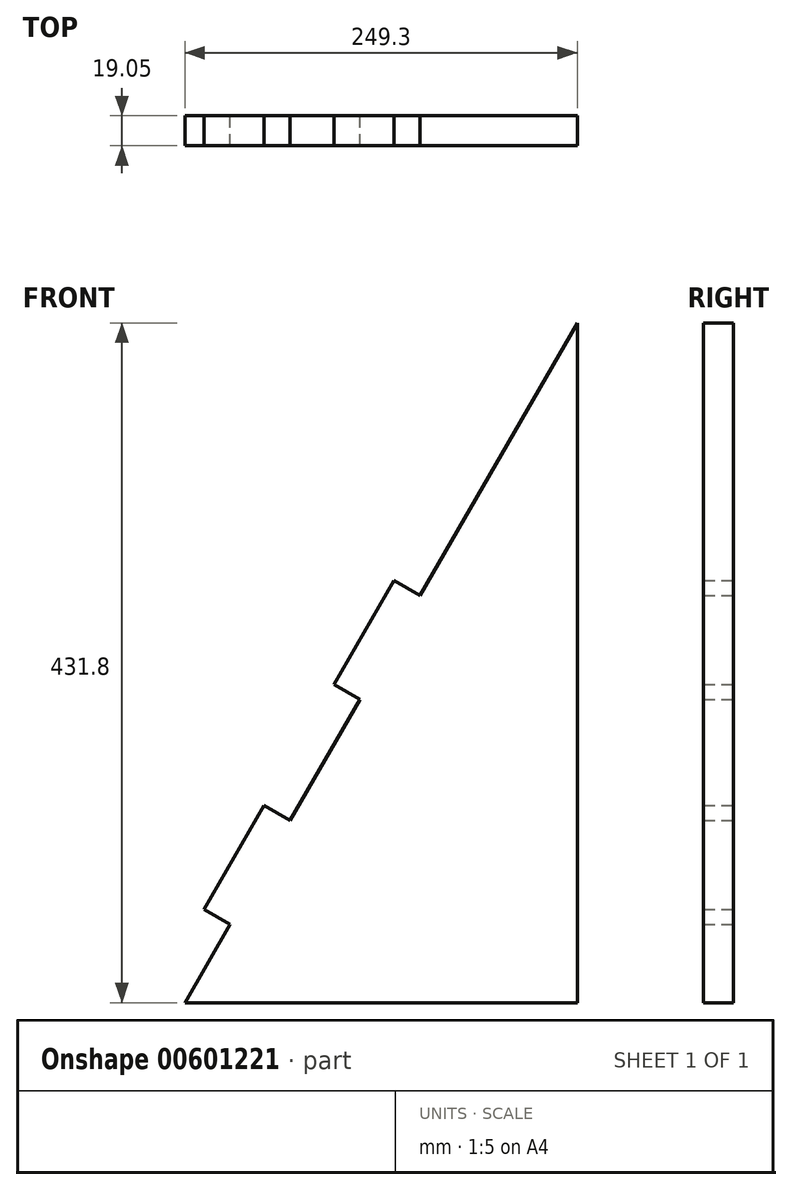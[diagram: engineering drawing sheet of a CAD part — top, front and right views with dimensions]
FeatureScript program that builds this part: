
annotation { "Feature Type Name" : "Feature", "Feature Type Description" : "" }
export const myFeature = defineFeature(function(context is Context, id is Id, definition is map)
    precondition{}
    {
        {
            var Q0;
            Q0=qCreatedBy(makeId("Front.planeOp"),FACE);
            var sketch = newSketch(context, id + "F0", { "sketchPlane" : qUnion([Q0])});
            skLineSegment(sketch, "E0", {"start": v(-193.97, -179.4) * mm, "end": v(-165.28, -129.7) * mm});
            skLineSegment(sketch, "E1", {"start": v(-193.97, -179.4) * mm, "end": v(-193.97, 147.18) * mm});
            skLineSegment(sketch, "E2", {"start": v(-193.97, -179.4) * mm, "end": v(55.33, -179.4) * mm});
            skLineSegment(sketch, "E3", {"start": v(-193.97, -179.4) * mm, "end": v(-270.91, -179.4) * mm});
            skLineSegment(sketch, "E4", {"start": v(270.41, -179.4) * mm, "end": v(270.41, 252.4) * mm});
            skLineSegment(sketch, "E5", {"start": v(17.02, 186.04) * mm, "end": v(55.33, 252.4) * mm});
            skLineSegment(sketch, "E6", {"start": v(270.41, 252.4) * mm, "end": v(55.33, 252.4) * mm});
            skLineSegment(sketch, "E7", {"start": v(55.33, 252.4) * mm, "end": v(55.33, -179.4) * mm});
            skLineSegment(sketch, "E8", {"start": v(-165.28, -129.7) * mm, "end": v(-181.77, -120.18) * mm});
            skLineSegment(sketch, "E9", {"start": v(-181.77, -120.18) * mm, "end": v(-143.67, -54.2) * mm});
            skLineSegment(sketch, "E10", {"start": v(-143.67, -54.2) * mm, "end": v(-127.18, -63.72) * mm});
            skLineSegment(sketch, "E11", {"start": v(-127.18, -63.72) * mm, "end": v(-82.73, 13.27) * mm});
            skLineSegment(sketch, "E12", {"start": v(-82.73, 13.27) * mm, "end": v(-99.22, 22.8) * mm});
            skLineSegment(sketch, "E13", {"start": v(-99.22, 22.8) * mm, "end": v(-61.12, 88.79) * mm});
            skLineSegment(sketch, "E14", {"start": v(-61.12, 88.79) * mm, "end": v(-44.63, 79.26) * mm});
            skLineSegment(sketch, "E15.trimOffspring", {"start": v(-44.63, 79.26) * mm, "end": v(17.02, 186.04) * mm});
            skSolve(sketch);
        }
        {
            var Q0;
            Q0=makeQuery(id+"F0.imprint","IMPRINT",FACE,{"disambiguationData":[TD([[makeQuery(id+"F0.imprint","IMPRINT",EDGE,{"derivedFrom":sQuery(id+"F0.wireOp",EDGE,"E2")}),1.0]])]});
            extrude(context, id + "F1", {"entities" : qUnion([Q0]), "depth" : 19.05 * mm, "offsetDistance" : 25.4 * mm});
        }
    });
